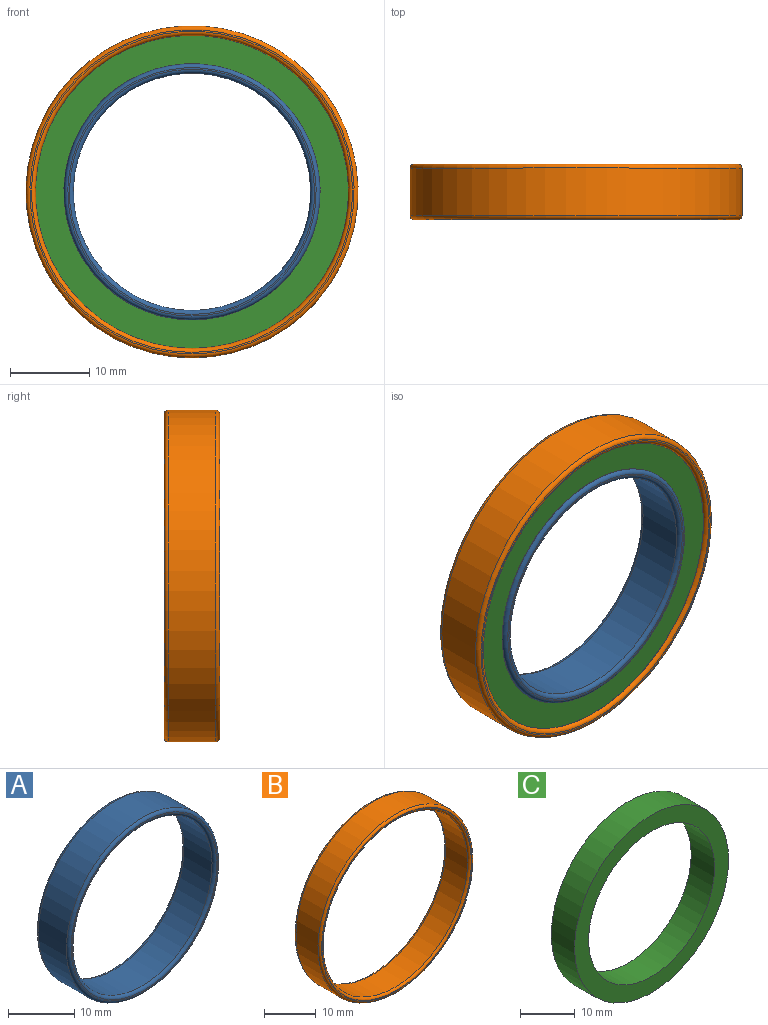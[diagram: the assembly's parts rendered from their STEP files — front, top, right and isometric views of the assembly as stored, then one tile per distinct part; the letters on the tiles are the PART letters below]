
ASSEMBLY  parts=3 mates=2
PART A: 8 faces, bbox 35.1x7x35.1 mm
  f0: cylinder r=15mm len=30mm, axis (0,1,0), area 565.5mm2, adj f4,f6
  f1: cylinder r=16.2mm len=32.4mm, axis (0,1,0), area 610.7mm2, adj f5,f7
  f2: plane 31.4x31.4mm, normal (0,-1,0), area 19.6mm2, adj f6,f7
  f3: plane 31.4x31.4mm, normal (0,1,0), area 19.6mm2, adj f4,f5
  f4: torus R=15.5mm, axis (0,-1,0), area 74.9mm2, adj f0,f3
  f5: torus R=15.7mm, axis (0,-1,0), area 79mm2, adj f1,f3
  f6: torus R=15.5mm, axis (0,-1,0), area 74.9mm2, adj f0,f2
  f7: torus R=15.7mm, axis (0,-1,0), area 79mm2, adj f1,f2
PART B: 8 faces, bbox 45.5x7x45.5 mm
  f0: cylinder r=19.8mm len=39.6mm, axis (0,1,0), area 746.4mm2, adj f5,f7
  f1: cylinder r=21mm len=42mm, axis (0,1,0), area 791.7mm2, adj f4,f6
  f2: plane 41x41mm, normal (0,-1,0), area 25.6mm2, adj f6,f7
  f3: plane 41x41mm, normal (0,1,0), area 25.6mm2, adj f4,f5
  f4: torus R=20.5mm, axis (0,-1,0), area 102.7mm2, adj f1,f3
  f5: torus R=20.3mm, axis (0,-1,0), area 98.6mm2, adj f0,f3
  f6: torus R=20.5mm, axis (0,-1,0), area 102.7mm2, adj f1,f2
  f7: torus R=20.3mm, axis (0,-1,0), area 98.6mm2, adj f0,f2
PART C: 4 faces, bbox 39.6x6x39.6 mm
  f0: cylinder r=16.2mm len=32.4mm, axis (0,1,0), area 610.7mm2, adj f2,f3
  f1: cylinder r=19.8mm len=39.6mm, axis (0,1,0), area 746.4mm2, adj f2,f3
  f2: plane 39.6x39.6mm, normal (0,-1,0), area 407.2mm2, adj f0,f1
  f3: plane 39.6x39.6mm, normal (0,1,0), area 407.2mm2, adj f0,f1
PLACE A t=(0.01,-0.02,-0.05)mm
PLACE B t=(0.01,-0.02,-0.05)mm
PLACE C t=(0.01,-0.02,-0.05)mm
MATE fastened A.f0 <-> C.f0  axis (0,1,0) through (0.01,-0.02,-0.05)mm
MATE fastened C.f0 <-> B.f0  axis (0,1,0) through (0.01,-0.02,-0.05)mm
